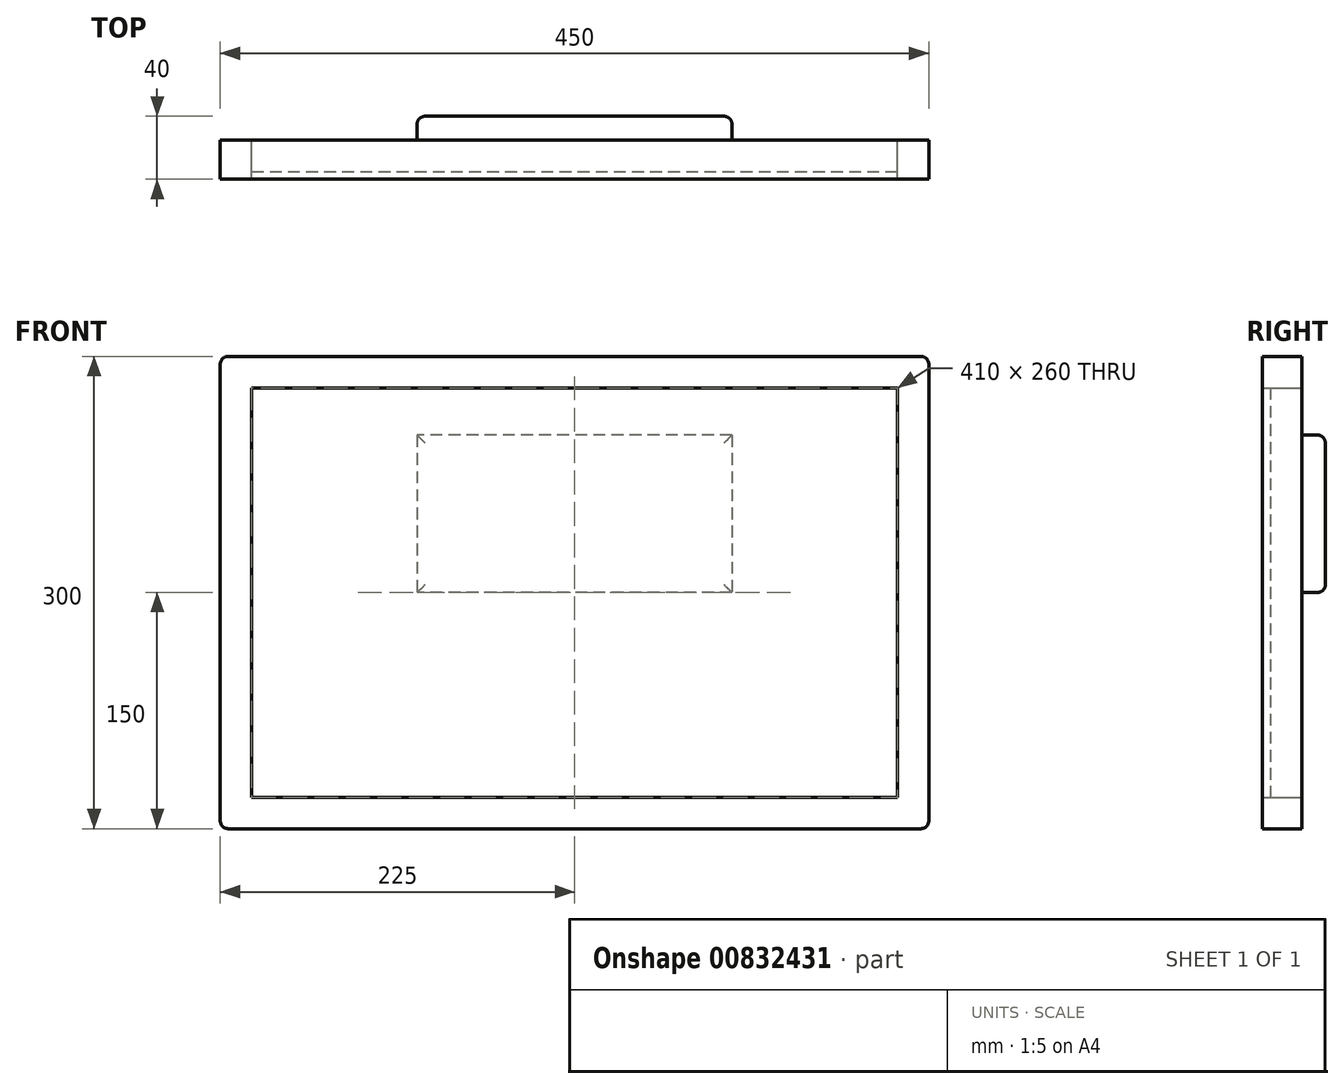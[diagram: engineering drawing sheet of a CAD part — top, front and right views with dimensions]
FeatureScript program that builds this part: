
annotation { "Feature Type Name" : "Feature", "Feature Type Description" : "" }
export const myFeature = defineFeature(function(context is Context, id is Id, definition is map)
    precondition{}
    {
        {
            var Q0;
            Q0=qCreatedBy(makeId("Front.planeOp"),FACE);
            var sketch = newSketch(context, id + "F0", { "sketchPlane" : qUnion([Q0])});
            skLineSegment(sketch, "E0.bottom", {"start": v(-225, 300) * mm, "end": v(225, 300) * mm});
            skLineSegment(sketch, "E0.top", {"start": v(-225, 0) * mm, "end": v(225, 0) * mm});
            skLineSegment(sketch, "E0.left", {"start": v(-225, 300) * mm, "end": v(-225, 0) * mm});
            skLineSegment(sketch, "E0.right", {"start": v(225, 300) * mm, "end": v(225, 0) * mm});
            skLineSegment(sketch, "E1.bottom", {"start": v(-205, 280) * mm, "end": v(205, 280) * mm});
            skLineSegment(sketch, "E1.top", {"start": v(-205, 20) * mm, "end": v(205, 20) * mm});
            skLineSegment(sketch, "E1.left", {"start": v(-205, 280) * mm, "end": v(-205, 20) * mm});
            skLineSegment(sketch, "E1.right", {"start": v(205, 280) * mm, "end": v(205, 20) * mm});
            skSolve(sketch);
        }
        {
            var Q0;
            Q0=makeQuery(id+"F0.imprint","IMPRINT",FACE,{"disambiguationData":[TD([[makeQuery(id+"F0.imprint","IMPRINT",EDGE,{"derivedFrom":sQuery(id+"F0.wireOp",EDGE,"E1.bottom")}),-1.0]])]});
            extrude(context, id + "F1", {"entities" : qUnion([Q0]), "depth" : 20 * mm, "offsetDistance" : 25 * mm});
        }
        {
            var Q0;
            Q0 = qSketchRegion(id + "F0", true);
            extrude(context, id + "F2", {"entities" : qUnion([Q0]), "depth" : 25 * mm, "offsetDistance" : 25 * mm});
        }
        {
            var Q0;
            Q0=makeQuery(id+"F2.opExtrude","SWEPT_EDGE",EDGE,{"disambiguationData":[OSD([sQuery(id+"F0.wireOp",EDGE,"E0.bottom"),sQuery(id+"F0.wireOp",EDGE,"E0.left")])]});
            var Q1;
            Q1=makeQuery(id+"F2.opExtrude","SWEPT_EDGE",EDGE,{"disambiguationData":[OSD([sQuery(id+"F0.wireOp",EDGE,"E0.bottom"),sQuery(id+"F0.wireOp",EDGE,"E0.right")])]});
            var Q2;
            Q2=makeQuery(id+"F2.opExtrude","SWEPT_EDGE",EDGE,{"disambiguationData":[OSD([sQuery(id+"F0.wireOp",EDGE,"E0.top"),sQuery(id+"F0.wireOp",EDGE,"E0.right")])]});
            var Q3;
            Q3=makeQuery(id+"F2.opExtrude","SWEPT_EDGE",EDGE,{"disambiguationData":[OSD([sQuery(id+"F0.wireOp",EDGE,"E0.top"),sQuery(id+"F0.wireOp",EDGE,"E0.left")])]});
            fillet(context, id + "F3", {"entities" : qUnion([Q0, Q1, Q2, Q3]), "radius" : 5 * mm, "tangentPropagation" : true, "allowEdgeOverflow" : false});
        }
        {
            var Q0;
            Q0=makeQuery(id+"F1.opExtrude","CAP_FACE",FACE,{"disambiguationData":[OSD([sQuery(id+"F0.wireOp",EDGE,"E1.bottom"),sQuery(id+"F0.wireOp",EDGE,"E1.top"),sQuery(id+"F0.wireOp",EDGE,"E1.left"),sQuery(id+"F0.wireOp",EDGE,"E1.right")])],"isStart":true});
            var sketch = newSketch(context, id + "F4", { "sketchPlane" : qUnion([Q0])});
            skLineSegment(sketch, "E2.bottom", {"start": v(-100, 250) * mm, "end": v(100, 250) * mm});
            skLineSegment(sketch, "E2.top", {"start": v(-100, 150) * mm, "end": v(100, 150) * mm});
            skLineSegment(sketch, "E2.left", {"start": v(-100, 250) * mm, "end": v(-100, 150) * mm});
            skLineSegment(sketch, "E2.right", {"start": v(100, 250) * mm, "end": v(100, 150) * mm});
            skSolve(sketch);
        }
        {
            var Q0;
            Q0 = qSketchRegion(id + "F4", true);
            extrude(context, id + "F5", {"entities" : qUnion([Q0]), "operationType" : NewBodyOperationType.ADD, "depth" : 15 * mm, "offsetDistance" : 25 * mm});
        }
        {
            var Q0;
            Q0=makeQuery(id+"F5.opExtrude","CAP_FACE",FACE,{"disambiguationData":[OSD([sQuery(id+"F4.wireOp",EDGE,"E2.bottom"),sQuery(id+"F4.wireOp",EDGE,"E2.top"),sQuery(id+"F4.wireOp",EDGE,"E2.left"),sQuery(id+"F4.wireOp",EDGE,"E2.right")])],"isStart":false});
            fillet(context, id + "F6", {"entities" : qUnion([Q0]), "radius" : 5 * mm, "tangentPropagation" : true, "allowEdgeOverflow" : false});
        }
    });
